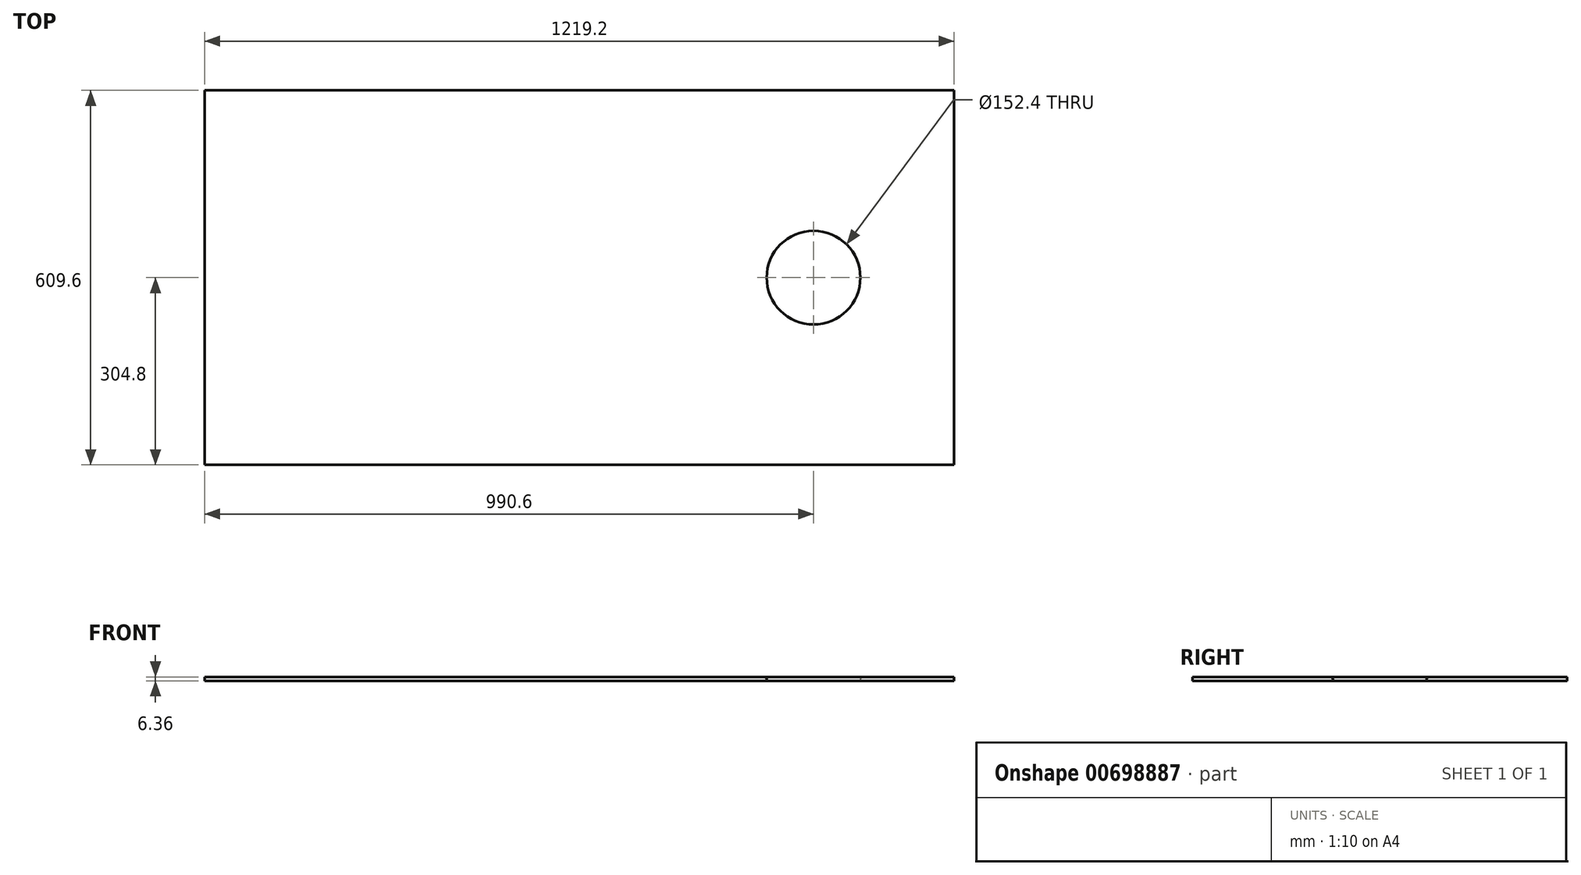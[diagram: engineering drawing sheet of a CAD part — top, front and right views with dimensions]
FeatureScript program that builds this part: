
annotation { "Feature Type Name" : "Feature", "Feature Type Description" : "" }
export const myFeature = defineFeature(function(context is Context, id is Id, definition is map)
    precondition{}
    {
        {
            var Q0;
            Q0=qCreatedBy(makeId("Top.planeOp"),FACE);
            var sketch = newSketch(context, id + "F0", { "sketchPlane" : qUnion([Q0])});
            skLineSegment(sketch, "E0.bottom", {"start": v(609.6, 304.8) * mm, "end": v(-609.6, 304.8) * mm});
            skLineSegment(sketch, "E0.top", {"start": v(609.6, -304.8) * mm, "end": v(-609.6, -304.8) * mm});
            skLineSegment(sketch, "E0.left", {"start": v(609.6, 304.8) * mm, "end": v(609.6, -304.8) * mm});
            skLineSegment(sketch, "E0.right", {"start": v(-609.6, 304.8) * mm, "end": v(-609.6, -304.8) * mm});
            skPoint(sketch, "E0.middle", {"position": v(0, 0) * mm});
            skCircle(sketch, "E1", {"center": v(381, 0) * mm, "radius": 76.2 * mm});
            skSolve(sketch);
        }
        {
            var Q0;
            Q0=makeQuery(id+"F0.imprint","IMPRINT",FACE,{"disambiguationData":[TD([[makeQuery(id+"F0.imprint","IMPRINT",EDGE,{"derivedFrom":sQuery(id+"F0.wireOp",EDGE,"E0.bottom")}),1.0]])]});
            extrude(context, id + "F1", {"entities" : qUnion([Q0]), "endBound" : BoundingType.SYMMETRIC, "depth" : 6.35 * mm, "offsetDistance" : 25.4 * mm});
        }
        {
            var Q0;
            Q0=makeQuery(id+"F1.opExtrude","CAP_EDGE",EDGE,{"disambiguationData":[OSD([sQuery(id+"F0.wireOp",EDGE,"E1")])],"isStart":false});
            fillet(context, id + "F2", {"entities" : qUnion([Q0]), "radius" : 4.7 * mm, "tangentPropagation" : true, "allowEdgeOverflow" : false});
        }
    });
